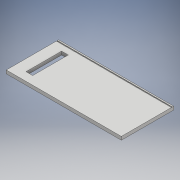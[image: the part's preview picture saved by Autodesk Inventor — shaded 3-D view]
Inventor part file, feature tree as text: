
AUTODESK INVENTOR PART (.ipt)
format: ipt  version: 2018.3 (Build 223284000, 284)  size: 125,952 bytes
history: native  units: mm
features: extrude x4, sketch x4
ambient origin geometry x8: Origin, YZ Plane, XZ Plane, XY Plane, X Axis, Y Axis, Z Axis, Center Point
bodies: Solid1 (feature_tree)
feature tree (8):
  extrude  "Extrusion1"  Depth=15.7mm
  extrude  "Extrusion3"  Depth=0.15mm
  extrude  "Extrusion4"  Depth=0.3mm TaperAngle=0.0deg
  extrude  "Extrusion5"  Depth=0.1mm
  sketch  "Sketch1"  dims[d0=34.5mm d1=15.7mm]
  sketch  "Sketch3"  dims[d2=1.0mm d3=0.0mm d8=0.15mm]
  sketch  "Sketch4"  dims[d9=0.3mm d10=40.0mm d11=0.0mm]
  sketch  "Sketch5"  dims[d12=0.4mm d13=0.1mm d14=0.15mm d15=0.0mm d16=2.0mm d17=0.0mm d18=2.0mm d19=10.660127mm d20=2.52mm d21=3.4mm]
